# Revit family: Ventüer_VentilationLouvres_VL-104D
name_source: partatom
category: Generic Models
units: mm (PartAtom-declared; Revit-internal decimal feet)

## family parameters
Always vertical = No
Can host rebar = No
Cut with Voids When Loaded = Yes
Part Type = Normal
Room Calculation Point = No
Round Connector Dimension = Use Diameter
Shared = No
Work Plane-Based = Yes

## types (3) — shared parameters
Aerodynamic Performance = Air Inlet: 0.317, Class 2. Air Extract: 0.317, Class 2
Ancillaries = Bird Mesh, Insect Mesh, Solid Blanking, Perimeter Mounting Angle
Blade Centres = 77 mm  [stored 0.252625 ft]
Blade Material = Ventüer Aluminium
Default Elevation = 1219 mm
Description = Drainable Single Bank Louvre
Exact Neck Height = 594 mm  [stored 1.94882 ft]
Exact Neck Height Check = 594 mm  [stored 1.94882 ft]
Exact Neck Width = 594 mm  [stored 1.94882 ft]
Exact Neck Width Check = 594 mm  [stored 1.94882 ft]
Frame Material = Ventüer Aluminium
Frame Set Count = 1
Frame Set Count Check = 2
Frame Set Transition Count = 1
Frame Set Transition Count Check = 2
Manufacturer = Ventüer
Max Flow = 5000.0 L/s
Min Flow = 100.0 L/s
Model = VL-104D
Multiple Frame Set = No
Multiple Transition = No
Noise Level NC Max = 0.00 NC
Noise Level NC Min = 0.00 NC
Nominal Height = 600 mm
Nominal Width = 600 mm
Nominated Air Flow = 100.0 L/s
Nominated Pessure Drop = 21.0 Pa
Rain Defence Performance = Class C - up to 1.0m/s suction velocity. Class D - up to 3.5m/s suction velocity
SHS = No
Single Frame Set = Yes
Single Transition = No
Specified Air Flow = 0.0 L/s
Specified Pressure Drop = 21.0 Pa
Static Pressure Max = 60.0 Pa
Static Pressure Min = 10.0 Pa
Tee = Yes
Top Blade = Yes
URL = https://www.ventuer.co
Ventüer Product Range = Ventilation Louvres

## per-type parameters (varying)
| type | Base Width | Blade And Frame Gap | Blade Count | Blade Cut Offset | Blade Offset | Channel | Connector Height | Connector Width | Depth | Flanged | Frame Set Width | Glazed | Overall Opening Height | Overall Opening Width | Profile Width | Screen Symbol Distance | Single Frame Set Width | Stiffener Length | Top Blade Corrector | Top Blade Height |
| VL-104D_CF | 3 mm  [stored 0.00984252 ft] | 20 mm  [stored 0.0656168 ft] | 7 | 540 mm | 6 mm  [stored 0.019685 ft] | Yes | 583 mm | 579 mm | 100 mm  [stored 0.328084 ft] | No | 579 mm | No | 583 mm | 579 mm | 8 mm  [stored 0.0262467 ft] | 4 mm  [stored 0.0131234 ft] | 289 mm | 588 mm  [stored 1.92913 ft] | 5 mm  [stored 0.0164042 ft] | 28 mm  [stored 0.0918635 ft] |
| VL-104D_GF | 26 mm | 6 mm  [stored 0.019685 ft] | 6 | 462 mm  [stored 1.51575 ft] | 9 mm  [stored 0.0295276 ft] | No | 532 mm | 521 mm | 105 mm  [stored 0.344488 ft] | No | 521 mm | Yes | 532 mm | 521 mm | 37 mm | 6 mm  [stored 0.019685 ft] | 261 mm | 542 mm | 11 mm | 74 mm |
| VL-104D_FF | 58 mm | 18 mm | 5 | 386 mm | 11 mm | No | 478 mm | 478 mm | 105 mm  [stored 0.344488 ft] | Yes | 478 mm | No | 478 mm | 478 mm | 58 mm | 5 mm  [stored 0.0164042 ft] | 239 mm | 478 mm | 0 mm  [stored 0 ft] | 75 mm |

note: column(s) folded — value = type name in every type: Keynote

note: [stored X ft] marks values corroborated as IEEE doubles in the binary element streams (Revit-internal decimal feet)

## geometry (parser evidence)
native form markers: Sweep x13
no freeform markers — native parametric forms only
